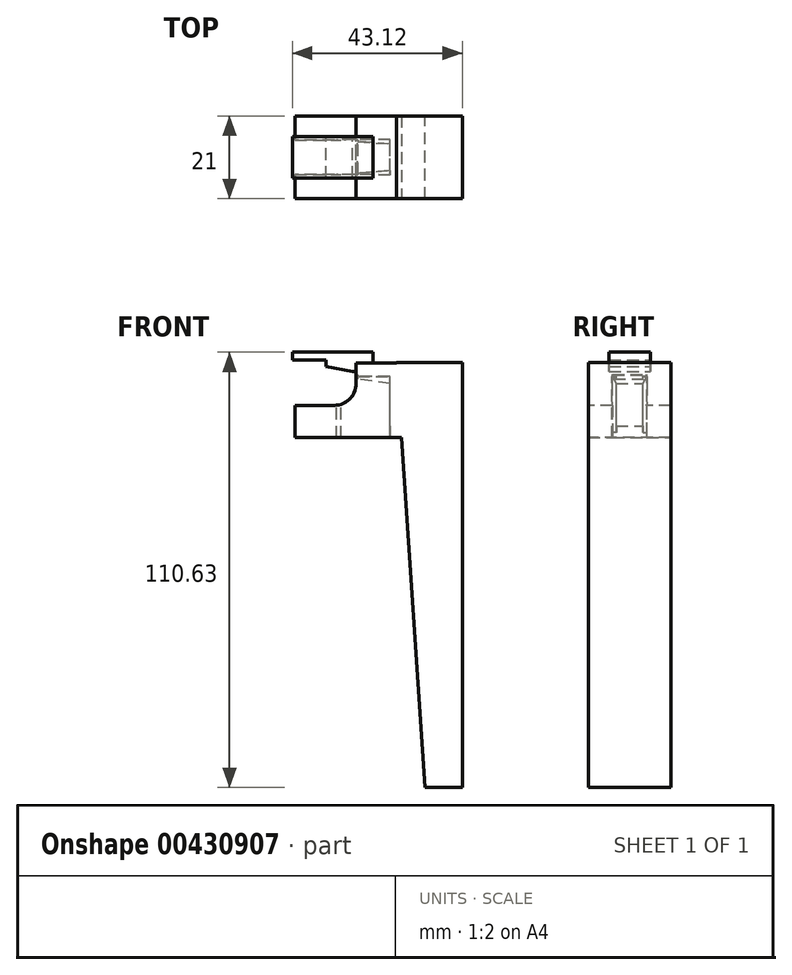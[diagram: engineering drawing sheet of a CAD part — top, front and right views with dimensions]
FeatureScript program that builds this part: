
annotation { "Feature Type Name" : "Feature", "Feature Type Description" : "" }
export const myFeature = defineFeature(function(context is Context, id is Id, definition is map)
    precondition{}
    {
        {
            var Q0;
            Q0=qCreatedBy(makeId("Front.planeOp"),FACE);
            var sketch = newSketch(context, id + "F0", { "sketchPlane" : qUnion([Q0])});
            skLineSegment(sketch, "E0.bottom", {"start": v(-55.85, 16) * mm, "end": v(-25.85, 16) * mm});
            skLineSegment(sketch, "E0.top", {"start": v(-55.85, -3) * mm, "end": v(-25.85, -3) * mm});
            skLineSegment(sketch, "E0.left", {"start": v(-55.85, 16) * mm, "end": v(-55.85, -3) * mm});
            skLineSegment(sketch, "E0.right", {"start": v(-25.85, 16) * mm, "end": v(-25.85, -3) * mm});
            skSolve(sketch);
        }
        {
            var Q0;
            Q0=qSketchRegion(id+"F0",true);
            extrude(context, id + "F1", {"entities" : qUnion([Q0]), "endBound" : BoundingType.SYMMETRIC, "depth" : 21 * mm});
        }
        {
            var Q0;
            Q0=qCreatedBy(makeId("Front.planeOp"),FACE);
            var sketch = newSketch(context, id + "F2", { "sketchPlane" : qUnion([Q0])});
            skLineSegment(sketch, "E1", {"start": v(-31.69, 0) * mm, "end": v(-31.69, 10.7) * mm});
            skLineSegment(sketch, "E2", {"start": v(-31.69, 0) * mm, "end": v(-56.29, 0) * mm});
            skPoint(sketch, "E3.endSnap0", {"position": v(-43.99, 0) * mm});
            skLineSegment(sketch, "E4", {"start": v(-31.69, 0) * mm, "end": v(-39.89, 0) * mm});
            skLineSegment(sketch, "E5", {"start": v(-39.86, 12.9) * mm, "end": v(-48.56, 12.9) * mm});
            skLineSegment(sketch, "E6", {"start": v(-48.59, 16.1) * mm, "end": v(-56.29, 16.1) * mm});
            skLineSegment(sketch, "E7", {"start": v(-56.29, 16.1) * mm, "end": v(-56.29, 0) * mm});
            skLineSegment(sketch, "E8", {"start": v(-48.56, 12.9) * mm, "end": v(-48.59, 16.1) * mm});
            skLineSegment(sketch, "E9", {"start": v(-31.69, 10.7) * mm, "end": v(-39.89, 11.82) * mm});
            skLineSegment(sketch, "E10", {"start": v(-39.86, 12.9) * mm, "end": v(-39.89, 11.82) * mm});
            skLineSegment(sketch, "E11", {"start": v(-48.57, 14.5) * mm, "end": v(-39.86, 12.9) * mm});
            skLineSegment(sketch, "E12", {"start": v(-56.29, 0) * mm, "end": v(-56.29, -4.06) * mm});
            skLineSegment(sketch, "E13", {"start": v(-56.29, -4.06) * mm, "end": v(-31.63, -4.06) * mm});
            skLineSegment(sketch, "E14", {"start": v(-31.69, 0) * mm, "end": v(-31.63, -4.06) * mm});
            skSolve(sketch);
        }
        {
            var Q0;
            Q0=qSketchRegion(id+"F2",true);
            extrude(context, id + "F3", {"entities" : qUnion([Q0]), "operationType" : NewBodyOperationType.REMOVE, "endBound" : BoundingType.SYMMETRIC, "depth" : 8.7 * mm});
        }
        {
            var Q0;
            Q0=qCreatedBy(makeId("Front.planeOp"),FACE);
            var sketch = newSketch(context, id + "F4", { "sketchPlane" : qUnion([Q0])});
            skLineSegment(sketch, "E15.bottom", {"start": v(-56.28, 16.09) * mm, "end": v(-45.78, 16.09) * mm});
            skLineSegment(sketch, "E15.top", {"start": v(-56.28, 5.19) * mm, "end": v(-45.78, 5.19) * mm});
            skLineSegment(sketch, "E15.left", {"start": v(-56.28, 16.09) * mm, "end": v(-56.28, 5.19) * mm});
            skPoint(sketch, "E16", {"position": v(-56.48, 10.64) * mm});
            skArc(sketch, "E17", {"start": v(-45.78, 5.19) * mm, "mid": v(-40.33, 10.64) * mm, "end": v(-45.78, 16.09) * mm});
            skLineSegment(sketch, "E18", {"start": v(-45.78, 16.09) * mm, "end": v(-40.33, 16.09) * mm});
            skPoint(sketch, "E18.endSnap0", {"position": v(-40.33, 10.64) * mm});
            skLineSegment(sketch, "E19", {"start": v(-40.33, 16.09) * mm, "end": v(-40.33, 10.64) * mm});
            skSolve(sketch);
        }
        {
            var Q0;
            Q0=qCreatedBy(makeId("Top.planeOp"),FACE);
            var sketch = newSketch(context, id + "F5", { "sketchPlane" : qUnion([Q0])});
            skLineSegment(sketch, "E20", {"start": v(-45.21, -4.43) * mm, "end": v(-31.66, -3.38) * mm});
            skLineSegment(sketch, "E21", {"start": v(-31.66, -3.38) * mm, "end": v(-31.66, -4.46) * mm});
            skLineSegment(sketch, "E22", {"start": v(-31.66, -4.46) * mm, "end": v(-45.21, -4.43) * mm});
            skLineSegment(sketch, "E23.MirrorCS", {"start": v(-45.21, 4.43) * mm, "end": v(-31.66, 3.38) * mm});
            skLineSegment(sketch, "E24.MirrorCS", {"start": v(-31.66, 4.46) * mm, "end": v(-45.21, 4.43) * mm});
            skLineSegment(sketch, "E25.MirrorCS", {"start": v(-31.66, 3.38) * mm, "end": v(-31.66, 4.46) * mm});
            skSolve(sketch);
        }
        {
            var Q0;
            Q0=qSketchRegion(id+"F5",true);
            extrude(context, id + "F6", {"entities" : qUnion([Q0]), "operationType" : NewBodyOperationType.REMOVE, "endBound" : BoundingType.SYMMETRIC, "oppositeDirection" : true, "depth" : 25 * mm, "hasSecondDirection" : true, "secondDirectionOppositeDirection" : true, "secondDirectionDepth" : 25 * mm});
        }
        {
            var Q0;
            Q0=qSketchRegion(id+"F4",true);
            var Q1;
            Q1=qConstructionFilter(qBodyType(qCreatedBy(id+"F4",EDGE),BodyType.WIRE),ConstructionObject.NO);
            extrude(context, id + "F7", {"entities" : qUnion([Q0]), "operationType" : NewBodyOperationType.REMOVE, "surfaceEntities" : qUnion([Q1]), "endBound" : BoundingType.SYMMETRIC, "depth" : 21 * mm});
        }
        {
            var Q0;
            Q0=qCreatedBy(makeId("Front.planeOp"),FACE);
            var sketch = newSketch(context, id + "F8", { "sketchPlane" : qUnion([Q0])});
            skLineSegment(sketch, "E26", {"start": v(-56.44, 18.7) * mm, "end": v(-36, 18.7) * mm});
            skLineSegment(sketch, "E27", {"start": v(-36, 18.7) * mm, "end": v(-36, 13.72) * mm});
            skLineSegment(sketch, "E28", {"start": v(-36, 13.72) * mm, "end": v(-41.19, 13.72) * mm});
            skLineSegment(sketch, "E29", {"start": v(-41.19, 13.72) * mm, "end": v(-47.93, 15.07) * mm});
            skLineSegment(sketch, "E30", {"start": v(-47.93, 15.07) * mm, "end": v(-47.93, 16.73) * mm});
            skLineSegment(sketch, "E31", {"start": v(-47.93, 16.73) * mm, "end": v(-56.44, 16.73) * mm});
            skLineSegment(sketch, "E32", {"start": v(-56.44, 16.73) * mm, "end": v(-56.44, 18.7) * mm});
            skSolve(sketch);
        }
        {
            var Q0;
            Q0=qSketchRegion(id+"F8",true);
            extrude(context, id + "F9", {"entities" : qUnion([Q0]), "operationType" : NewBodyOperationType.ADD, "endBound" : BoundingType.SYMMETRIC, "depth" : 10.5 * mm});
        }
        {
            var Q0;
            Q0=qCreatedBy(makeId("Front.planeOp"),FACE);
            var sketch = newSketch(context, id + "F10", { "sketchPlane" : qUnion([Q0])});
            skLineSegment(sketch, "E33", {"start": v(-25.82, 16.08) * mm, "end": v(-13.32, 16.08) * mm});
            skLineSegment(sketch, "E34", {"start": v(-13.32, 16.08) * mm, "end": v(-13.32, -91.92) * mm});
            skLineSegment(sketch, "E35", {"start": v(-13.32, -91.92) * mm, "end": v(-22.82, -91.92) * mm});
            skLineSegment(sketch, "E36", {"start": v(-22.82, -91.92) * mm, "end": v(-30.08, 16.08) * mm});
            skLineSegment(sketch, "E37", {"start": v(-30.08, 16.08) * mm, "end": v(-25.82, 16.08) * mm});
            skSolve(sketch);
        }
        {
            var Q0;
            Q0 = qSketchRegion(id + "F10", true);
            extrude(context, id + "F11", {"entities" : qUnion([Q0]), "operationType" : NewBodyOperationType.ADD, "endBound" : BoundingType.SYMMETRIC, "depth" : 21 * mm});
        }
    });
